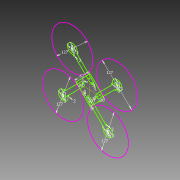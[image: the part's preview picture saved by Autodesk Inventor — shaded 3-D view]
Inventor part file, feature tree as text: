
AUTODESK INVENTOR PART (.ipt)
format: ipt  version: 2015 (Build 190159000, 159)  size: 116,224 bytes
history: native  units: mm
features: sketch x1
ambient origin geometry x8: Origin, YZ Plane, XZ Plane, XY Plane, X Axis, Y Axis, Z Axis, Center Point
feature tree (1):
  sketch  "Sketch1"  dims[d2=3.0mm d3=3.0mm d4=3.0mm d5=3.0mm d9=62.0mm d13=3.0mm d14=3.0mm d15=3.0mm d16=6.0mm d17=2.0mm d18=3.0mm d19=3.0mm d20=3.0mm d21=6.0mm d22=2.0mm d23=3.0mm d24=3.0mm d25=3.0mm d26=6.0mm d27=2.0mm d28=3.0mm d29=3.0mm d30=3.0mm d31=6.0mm d32=2.0mm d34=20.0mm d35=5.0mm d36=20.0mm d37=20.0mm d38=127.0mm d39=127.0mm d40=127.0mm d41=127.0mm]
